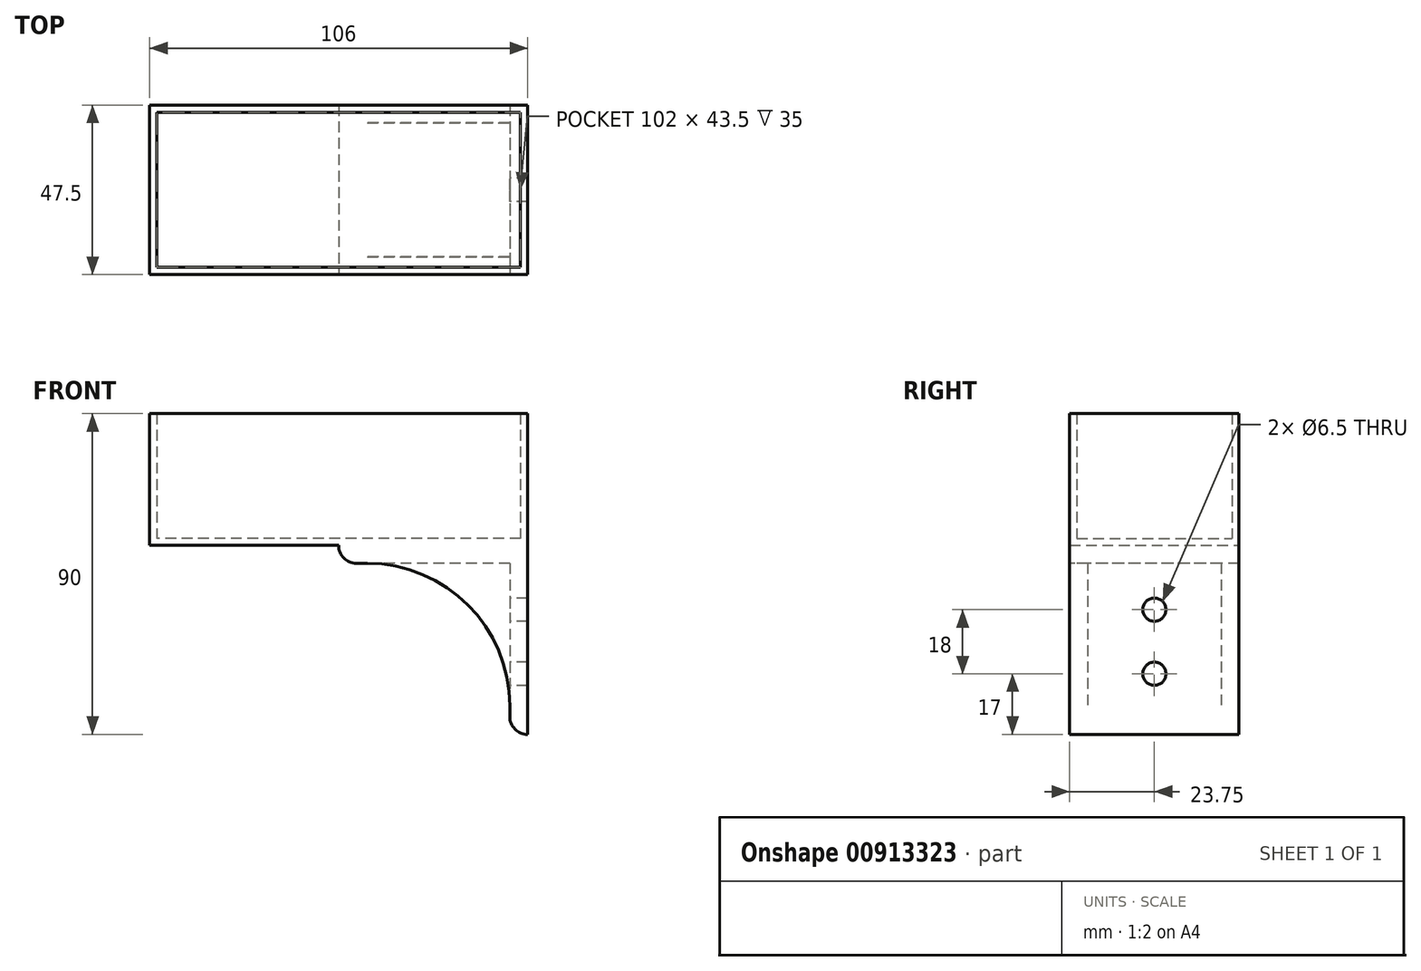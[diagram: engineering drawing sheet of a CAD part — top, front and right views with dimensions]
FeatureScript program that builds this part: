
annotation { "Feature Type Name" : "Feature", "Feature Type Description" : "" }
export const myFeature = defineFeature(function(context is Context, id is Id, definition is map)
    precondition{}
    {
        {
            var Q0;
            Q0=qCreatedBy(makeId("Top.planeOp"),FACE);
            var sketch = newSketch(context, id + "F0", { "sketchPlane" : qUnion([Q0])});
            skLineSegment(sketch, "E0.bottom", {"start": v(51, -21.75) * mm, "end": v(-51, -21.75) * mm});
            skLineSegment(sketch, "E0.top", {"start": v(51, 21.75) * mm, "end": v(-51, 21.75) * mm});
            skLineSegment(sketch, "E0.left", {"start": v(51, -21.75) * mm, "end": v(51, 21.75) * mm});
            skLineSegment(sketch, "E0.right", {"start": v(-51, -21.75) * mm, "end": v(-51, 21.75) * mm});
            skPoint(sketch, "E0.middle", {"position": v(0, 0) * mm});
            skLineSegment(sketch, "E1.0", {"start": v(53, 23.75) * mm, "end": v(-53, 23.75) * mm});
            skLineSegment(sketch, "E1.1", {"start": v(53, -23.75) * mm, "end": v(53, 23.75) * mm});
            skLineSegment(sketch, "E1.2", {"start": v(53, -23.75) * mm, "end": v(-53, -23.75) * mm});
            skLineSegment(sketch, "E1.3", {"start": v(-53, -23.75) * mm, "end": v(-53, 23.75) * mm});
            skSolve(sketch);
        }
        {
            var Q0;
            Q0=makeQuery(id+"F0.imprint","IMPRINT",FACE,{"disambiguationData":[TD([[makeQuery(id+"F0.imprint","IMPRINT",EDGE,{"derivedFrom":sQuery(id+"F0.wireOp",EDGE,"E0.bottom")}),1.0]])]});
            var Q1;
            Q1=makeQuery(id+"F0.imprint","IMPRINT",FACE,{"disambiguationData":[TD([[makeQuery(id+"F0.imprint","IMPRINT",EDGE,{"derivedFrom":sQuery(id+"F0.wireOp",EDGE,"E0.bottom")}),-1.0]])]});
            extrude(context, id + "F1", {"entities" : qUnion([Q0, Q1]), "depth" : 2 * mm, "offsetDistance" : 25 * mm});
        }
        {
            var Q0;
            Q0=makeQuery(id+"F1.opExtrude","CAP_FACE",FACE,{"disambiguationData":[OSD([sQuery(id+"F0.wireOp",EDGE,"E1.0"),sQuery(id+"F0.wireOp",EDGE,"E1.1"),sQuery(id+"F0.wireOp",EDGE,"E1.2"),sQuery(id+"F0.wireOp",EDGE,"E1.3")])],"isStart":false});
            var sketch = newSketch(context, id + "F2", { "sketchPlane" : qUnion([Q0])});
            skLineSegment(sketch, "E2.bottom", {"start": v(53, -23.75) * mm, "end": v(-53, -23.75) * mm});
            skLineSegment(sketch, "E2.top", {"start": v(53, 23.75) * mm, "end": v(-53, 23.75) * mm});
            skLineSegment(sketch, "E2.left", {"start": v(53, -23.75) * mm, "end": v(53, 23.75) * mm});
            skLineSegment(sketch, "E2.right", {"start": v(-53, -23.75) * mm, "end": v(-53, 23.75) * mm});
            skPoint(sketch, "E2.middle", {"position": v(0, 0) * mm});
            skLineSegment(sketch, "E3.0", {"start": v(51, 21.75) * mm, "end": v(-51, 21.75) * mm});
            skLineSegment(sketch, "E3.1", {"start": v(51, -21.75) * mm, "end": v(51, 21.75) * mm});
            skLineSegment(sketch, "E3.2", {"start": v(51, -21.75) * mm, "end": v(-51, -21.75) * mm});
            skLineSegment(sketch, "E3.3", {"start": v(-51, -21.75) * mm, "end": v(-51, 21.75) * mm});
            skSolve(sketch);
        }
        {
            var Q0;
            Q0=makeQuery(id+"F2.imprint","IMPRINT",FACE,{"disambiguationData":[TD([[makeQuery(id+"F2.imprint","IMPRINT",EDGE,{"derivedFrom":sQuery(id+"F2.wireOp",EDGE,"E2.bottom")}),-1.0]])]});
            extrude(context, id + "F3", {"entities" : qUnion([Q0]), "operationType" : NewBodyOperationType.ADD, "depth" : 35 * mm, "offsetDistance" : 25 * mm});
        }
        {
            var Q0;
            Q0=makeQuery(id+"F3.boolean.opBoolean","MERGE",FACE,{"derivedFrom":[makeQuery(id+"F1.opExtrude","SWEPT_FACE",FACE,{"disambiguationData":[OSD([sQuery(id+"F0.wireOp",EDGE,"E1.2")])]}),makeQuery(id+"F3.opExtrude","SWEPT_FACE",FACE,{"disambiguationData":[OSD([sQuery(id+"F2.wireOp",EDGE,"E2.bottom")])]})]});
            var sketch = newSketch(context, id + "F4", { "sketchPlane" : qUnion([Q0])});
            skLineSegment(sketch, "E4", {"start": v(53, 0) * mm, "end": v(53, -53) * mm});
            skLineSegment(sketch, "E5.0", {"start": v(48, -45) * mm, "end": v(48, -48) * mm});
            skLineSegment(sketch, "E6", {"start": v(53, -53) * mm, "end": v(53, -53) * mm});
            skLineSegment(sketch, "E7.bottom", {"start": v(53, 0) * mm, "end": v(0, 0) * mm});
            skLineSegment(sketch, "E7.top", {"start": v(8, -5) * mm, "end": v(5, -5) * mm});
            skLineSegment(sketch, "E7.left", {"start": v(53, 0) * mm, "end": v(53, -5) * mm});
            skLineSegment(sketch, "E7.right", {"start": v(0, 0) * mm, "end": v(0, 0) * mm});
            skPoint(sketch, "E8.visualSharp", {"position": v(48, -5) * mm});
            skArc(sketch, "E8.filletArc", {"start": v(48, -45) * mm, "mid": v(36.28, -16.72) * mm, "end": v(8, -5) * mm});
            skPoint(sketch, "E9.visualSharp", {"position": v(0, -5) * mm});
            skArc(sketch, "E9.filletArc", {"start": v(0, 0) * mm, "mid": v(1.46, -3.54) * mm, "end": v(5, -5) * mm});
            skPoint(sketch, "E10.visualSharp", {"position": v(48, -53) * mm});
            skArc(sketch, "E10.filletArc", {"start": v(48, -48) * mm, "mid": v(49.46, -51.54) * mm, "end": v(53, -53) * mm});
            skSolve(sketch);
        }
        {
            var Q0;
            Q0=makeQuery(id+"F4.imprint","IMPRINT",FACE,{"disambiguationData":[TD([[makeQuery(id+"F4.imprint","IMPRINT",EDGE,{"derivedFrom":sQuery(id+"F4.wireOp",EDGE,"E4")}),-1.0]])]});
            extrude(context, id + "F5", {"entities" : qUnion([Q0]), "operationType" : NewBodyOperationType.ADD, "oppositeDirection" : true, "depth" : 47.5 * mm, "offsetDistance" : 25 * mm});
        }
        {
            var Q0;
            Q0=makeQuery(id+"F3.boolean.opBoolean","MERGE",FACE,{"derivedFrom":[makeQuery(id+"F1.opExtrude","SWEPT_FACE",FACE,{"disambiguationData":[OSD([sQuery(id+"F0.wireOp",EDGE,"E1.3")])]}),makeQuery(id+"F3.opExtrude","SWEPT_FACE",FACE,{"disambiguationData":[OSD([sQuery(id+"F2.wireOp",EDGE,"E2.right")])]})]});
            var sketch = newSketch(context, id + "F6", { "sketchPlane" : qUnion([Q0])});
            skLineSegment(sketch, "E11.bottom", {"start": v(18.75, 0) * mm, "end": v(-18.75, 0) * mm});
            skLineSegment(sketch, "E11.top", {"start": v(18.75, -53) * mm, "end": v(-18.75, -53) * mm});
            skLineSegment(sketch, "E11.left", {"start": v(18.75, 0) * mm, "end": v(18.75, -53) * mm});
            skLineSegment(sketch, "E11.right", {"start": v(-18.75, 0) * mm, "end": v(-18.75, -53) * mm});
            skLineSegment(sketch, "E12", {"start": v(-18.75, -5) * mm, "end": v(18.75, -5) * mm});
            skSolve(sketch);
        }
        {
            var Q0;
            {var subQ0=sQuery(id+"F6.wireOp",EDGE,"E11.top");Q0=makeQuery(id+"F6.imprint","IMPRINT",FACE,{"disambiguationData":[TD([[makeQuery(id+"F6.imprint","IMPRINT",EDGE,{"derivedFrom":subQ0}),-1.0]])]});}
            extrude(context, id + "F7", {"entities" : qUnion([Q0]), "operationType" : NewBodyOperationType.REMOVE, "oppositeDirection" : true, "depth" : 101 * mm, "offsetDistance" : 25 * mm});
        }
        {
            var Q0;
            Q0=makeQuery(id+"F7.boolean.opBoolean","MERGE",FACE,{"derivedFrom":[makeQuery(id+"F5.opExtrude","SWEPT_FACE",FACE,{"disambiguationData":[OSD([sQuery(id+"F4.wireOp",EDGE,"E5.0")])]})],"fromTools":[makeQuery(id+"F7.opExtrude","CAP_FACE",FACE,{"disambiguationData":[OSD([sQuery(id+"F6.wireOp",EDGE,"E11.top"),sQuery(id+"F6.wireOp",EDGE,"E11.left"),sQuery(id+"F6.wireOp",EDGE,"E11.right"),sQuery(id+"F6.wireOp",EDGE,"E12")])],"isStart":false})]});
            var sketch = newSketch(context, id + "F8", { "sketchPlane" : qUnion([Q0])});
            skCircle(sketch, "E13", {"center": v(0, -18) * mm, "radius": 3.25 * mm});
            skCircle(sketch, "E14", {"center": v(0, -36) * mm, "radius": 3.25 * mm});
            skSolve(sketch);
        }
        {
            var Q0;
            Q0=makeQuery(id+"F8.imprint","IMPRINT",FACE,{"disambiguationData":[TD([[makeQuery(id+"F8.imprint","IMPRINT",EDGE,{"derivedFrom":sQuery(id+"F8.wireOp",EDGE,"E13")}),1.0]])]});
            var Q1;
            Q1=makeQuery(id+"F8.imprint","IMPRINT",FACE,{"disambiguationData":[TD([[makeQuery(id+"F8.imprint","IMPRINT",EDGE,{"derivedFrom":sQuery(id+"F8.wireOp",EDGE,"E14")}),1.0]])]});
            extrude(context, id + "F9", {"entities" : qUnion([Q0, Q1]), "operationType" : NewBodyOperationType.REMOVE, "oppositeDirection" : true, "depth" : 25 * mm, "offsetDistance" : 25 * mm});
        }
    });
